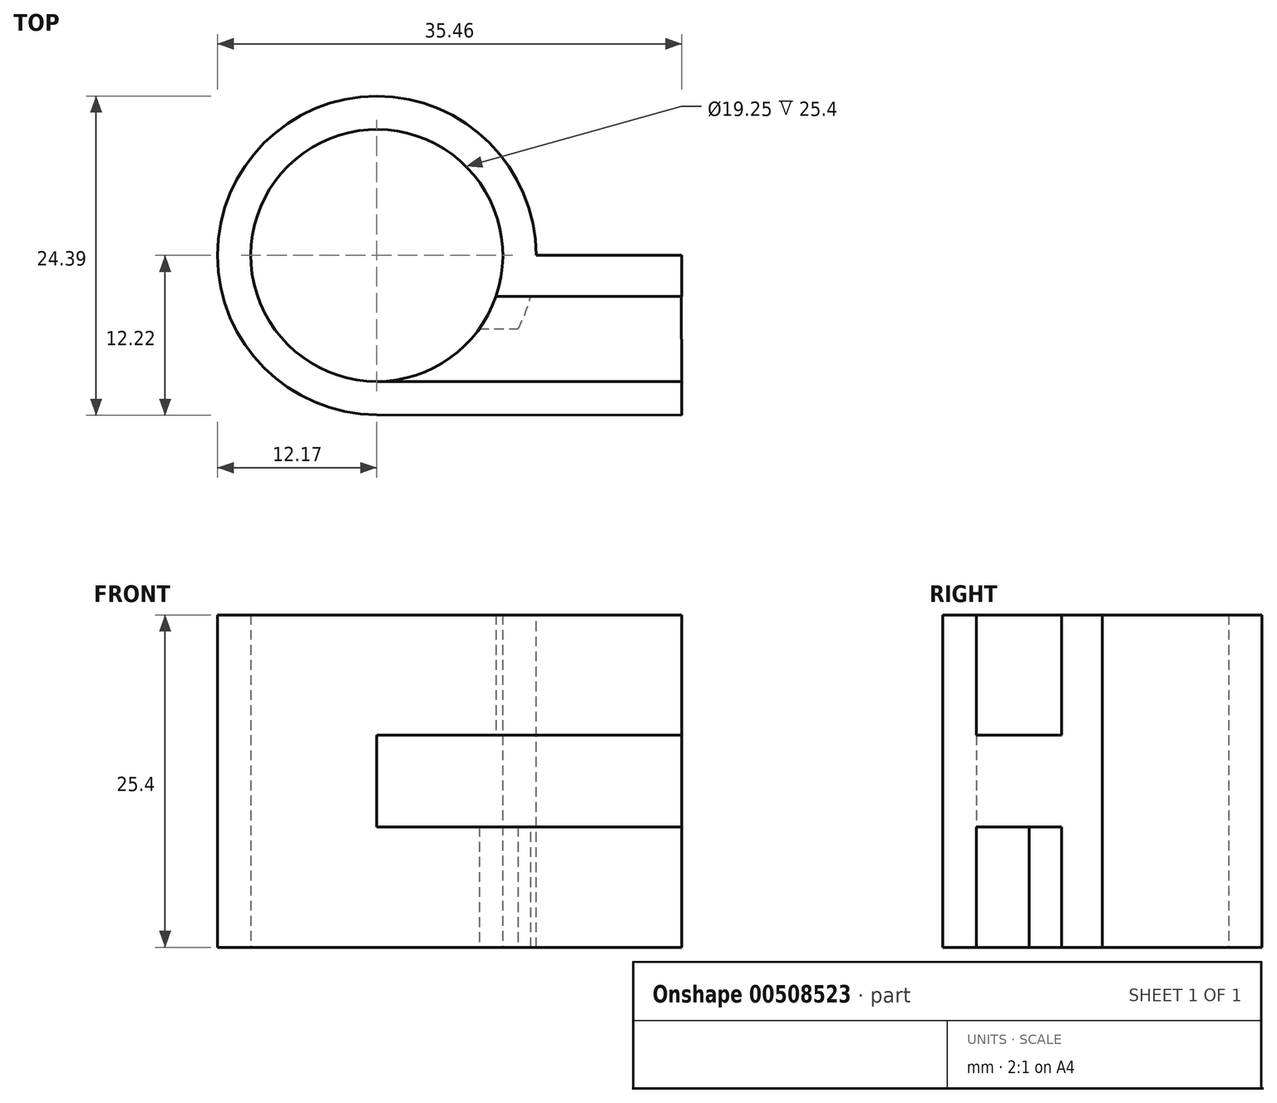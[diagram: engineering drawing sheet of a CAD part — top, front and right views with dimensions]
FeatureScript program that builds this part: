
annotation { "Feature Type Name" : "Feature", "Feature Type Description" : "" }
export const myFeature = defineFeature(function(context is Context, id is Id, definition is map)
    precondition{}
    {
        {
            var Q0;
            Q0=qCreatedBy(makeId("Top.planeOp"),FACE);
            var sketch = newSketch(context, id + "F0", { "sketchPlane" : qUnion([Q0])});
            skCircle(sketch, "E0", {"center": v(0, 0) * mm, "radius": 12.17 * mm});
            skCircle(sketch, "E1", {"center": v(0, 0) * mm, "radius": 9.63 * mm});
            skSolve(sketch);
        }
        {
            var Q0;
            Q0 = qSketchRegion(id + "F0", true);
            extrude(context, id + "F1", {"entities" : qUnion([Q0]), "depth" : 25.4 * mm});
        }
        {
            var Q0;
            Q0=makeQuery(id+"F1.opExtrude","CAP_FACE",FACE,{"disambiguationData":[OSD([sQuery(id+"F0.wireOp",EDGE,"E0"),sQuery(id+"F0.wireOp",EDGE,"E1")])],"isStart":false});
            var sketch = newSketch(context, id + "F2", { "sketchPlane" : qUnion([Q0])});
            skLineSegment(sketch, "E2", {"start": v(0, -12.17) * mm, "end": v(20.78, -12.17) * mm});
            skLineSegment(sketch, "E3", {"start": v(20.78, -12.17) * mm, "end": v(20.78, -3.13) * mm});
            skLineSegment(sketch, "E4", {"start": v(20.78, -3.13) * mm, "end": v(0, -3.13) * mm});
            skLineSegment(sketch, "E5", {"start": v(0, -12.17) * mm, "end": v(0, -3.13) * mm});
            skSolve(sketch);
        }
        {
            var Q0;
            {var subQ0=sQuery(id+"F2.wireOp",EDGE,"E2");Q0=makeQuery(id+"F2.imprint","IMPRINT",FACE,{"disambiguationData":[TD([[makeQuery(id+"F2.imprint","IMPRINT",EDGE,{"derivedFrom":subQ0}),1.0]])]});}
            var Q1;
            Q1 = qSketchRegion(id + "F2", true);
            extrude(context, id + "F3", {"entities" : qUnion([Q0, Q1]), "operationType" : NewBodyOperationType.REMOVE, "oppositeDirection" : true, "depth" : 9.2 * mm});
        }
        {
            var Q0;
            Q0=makeQuery(id+"F1.opExtrude","CAP_FACE",FACE,{"disambiguationData":[OSD([sQuery(id+"F0.wireOp",EDGE,"E0"),sQuery(id+"F0.wireOp",EDGE,"E1")])],"isStart":true});
            var sketch = newSketch(context, id + "F4", { "sketchPlane" : qUnion([Q0])});
            skLineSegment(sketch, "E6", {"start": v(0, 5.62) * mm, "end": v(13.36, 5.62) * mm});
            skLineSegment(sketch, "E7", {"start": v(0, 12.17) * mm, "end": v(13.36, 12.17) * mm});
            skLineSegment(sketch, "E8", {"start": v(13.36, 5.62) * mm, "end": v(13.36, 12.17) * mm});
            skLineSegment(sketch, "E9", {"start": v(0, 12.17) * mm, "end": v(0, 5.62) * mm});
            skSolve(sketch);
        }
        {
            var Q0;
            Q0 = qSketchRegion(id + "F4", true);
            extrude(context, id + "F5", {"entities" : qUnion([Q0]), "operationType" : NewBodyOperationType.REMOVE, "oppositeDirection" : true, "depth" : 9.2 * mm});
        }
        {
            var Q0;
            Q0=makeQuery(id+"F1.opExtrude","CAP_FACE",FACE,{"disambiguationData":[OSD([sQuery(id+"F0.wireOp",EDGE,"E0"),sQuery(id+"F0.wireOp",EDGE,"E1")])],"isStart":false});
            var sketch = newSketch(context, id + "F6", { "sketchPlane" : qUnion([Q0])});
            skLineSegment(sketch, "E10", {"start": v(23.28, -3.13) * mm, "end": v(10.87, -3.13) * mm});
            skLineSegment(sketch, "E11", {"start": v(0, -9.63) * mm, "end": v(23.28, -9.63) * mm});
            skLineSegment(sketch, "E12", {"start": v(23.28, -9.63) * mm, "end": v(23.28, -12.2) * mm});
            skLineSegment(sketch, "E13", {"start": v(23.28, -12.2) * mm, "end": v(0, -12.17) * mm});
            skLineSegment(sketch, "E14", {"start": v(0, -12.17) * mm, "end": v(0, -9.63) * mm});
            skLineSegment(sketch, "E15", {"start": v(23.28, -3.13) * mm, "end": v(23.28, 0) * mm});
            skLineSegment(sketch, "E16", {"start": v(23.28, 0) * mm, "end": v(12.17, 0) * mm});
            skLineSegment(sketch, "E17", {"start": v(10.87, -3.13) * mm, "end": v(12.17, 0) * mm});
            skSolve(sketch);
        }
        {
            var Q0;
            {var subQ0=sQuery(id+"F6.wireOp",EDGE,"E15");Q0=makeQuery(id+"F6.imprint","IMPRINT",FACE,{"disambiguationData":[TD([[makeQuery(id+"F6.imprint","IMPRINT",EDGE,{"derivedFrom":subQ0}),1.0]])]});}
            var Q1;
            Q1=makeQuery(id+"F6.imprint","IMPRINT",FACE,{"disambiguationData":[TD([[makeQuery(id+"F6.imprint","IMPRINT",EDGE,{"derivedFrom":sQuery(id+"F6.wireOp",EDGE,"E11")}),-1.0]])]});
            var Q2;
            Q2=makeQuery(id+"F1.opExtrude","CAP_FACE",FACE,{"disambiguationData":[OSD([sQuery(id+"F0.wireOp",EDGE,"E0"),sQuery(id+"F0.wireOp",EDGE,"E1")])],"isStart":true});
            extrude(context, id + "F7", {"entities" : qUnion([Q0, Q1]), "operationType" : NewBodyOperationType.ADD, "endBound" : BoundingType.UP_TO_SURFACE, "oppositeDirection" : true, "endBoundEntityFace" : qUnion([Q2]), "depth" : 25.4 * mm});
        }
        {
            var Q0;
            Q0=makeQuery(id+"F3.boolean.opBoolean","COPY",FACE,{"derivedFrom":makeQuery(id+"F3.opExtrude","CAP_FACE",FACE,{"disambiguationData":[OSD([sQuery(id+"F2.wireOp",EDGE,"E2"),sQuery(id+"F2.wireOp",EDGE,"E3"),sQuery(id+"F2.wireOp",EDGE,"E4"),sQuery(id+"F2.wireOp",EDGE,"E5")])],"isStart":false})});
            var sketch = newSketch(context, id + "F8", { "sketchPlane" : qUnion([Q0])});
            skLineSegment(sketch, "E18", {"start": v(0, -12.17) * mm, "end": v(23.29, -12.22) * mm});
            skLineSegment(sketch, "E19", {"start": v(11.82, -2.81) * mm, "end": v(0, -12.17) * mm});
            skLineSegment(sketch, "E20", {"start": v(11.82, -2.81) * mm, "end": v(23.28, -2.81) * mm});
            skLineSegment(sketch, "E21", {"start": v(23.29, -12.22) * mm, "end": v(23.28, -2.81) * mm});
            skSolve(sketch);
        }
        {
            var Q0;
            Q0=makeQuery(id+"F8.imprint","IMPRINT",FACE,{"disambiguationData":[TD([[makeQuery(id+"F8.imprint","IMPRINT",EDGE,{"derivedFrom":sQuery(id+"F8.wireOp",EDGE,"E18")}),1.0]])]});
            var Q1;
            Q1=makeQuery(id+"F5.boolean.opBoolean","COPY",FACE,{"derivedFrom":makeQuery(id+"F5.opExtrude","CAP_FACE",FACE,{"disambiguationData":[OSD([sQuery(id+"F4.wireOp",EDGE,"E6"),sQuery(id+"F4.wireOp",EDGE,"E7"),sQuery(id+"F4.wireOp",EDGE,"E8"),sQuery(id+"F4.wireOp",EDGE,"E9")])],"isStart":false})});
            extrude(context, id + "F9", {"entities" : qUnion([Q0]), "operationType" : NewBodyOperationType.ADD, "endBound" : BoundingType.UP_TO_SURFACE, "oppositeDirection" : true, "endBoundEntityFace" : qUnion([Q1]), "depth" : 25.4 * mm});
        }
    });
